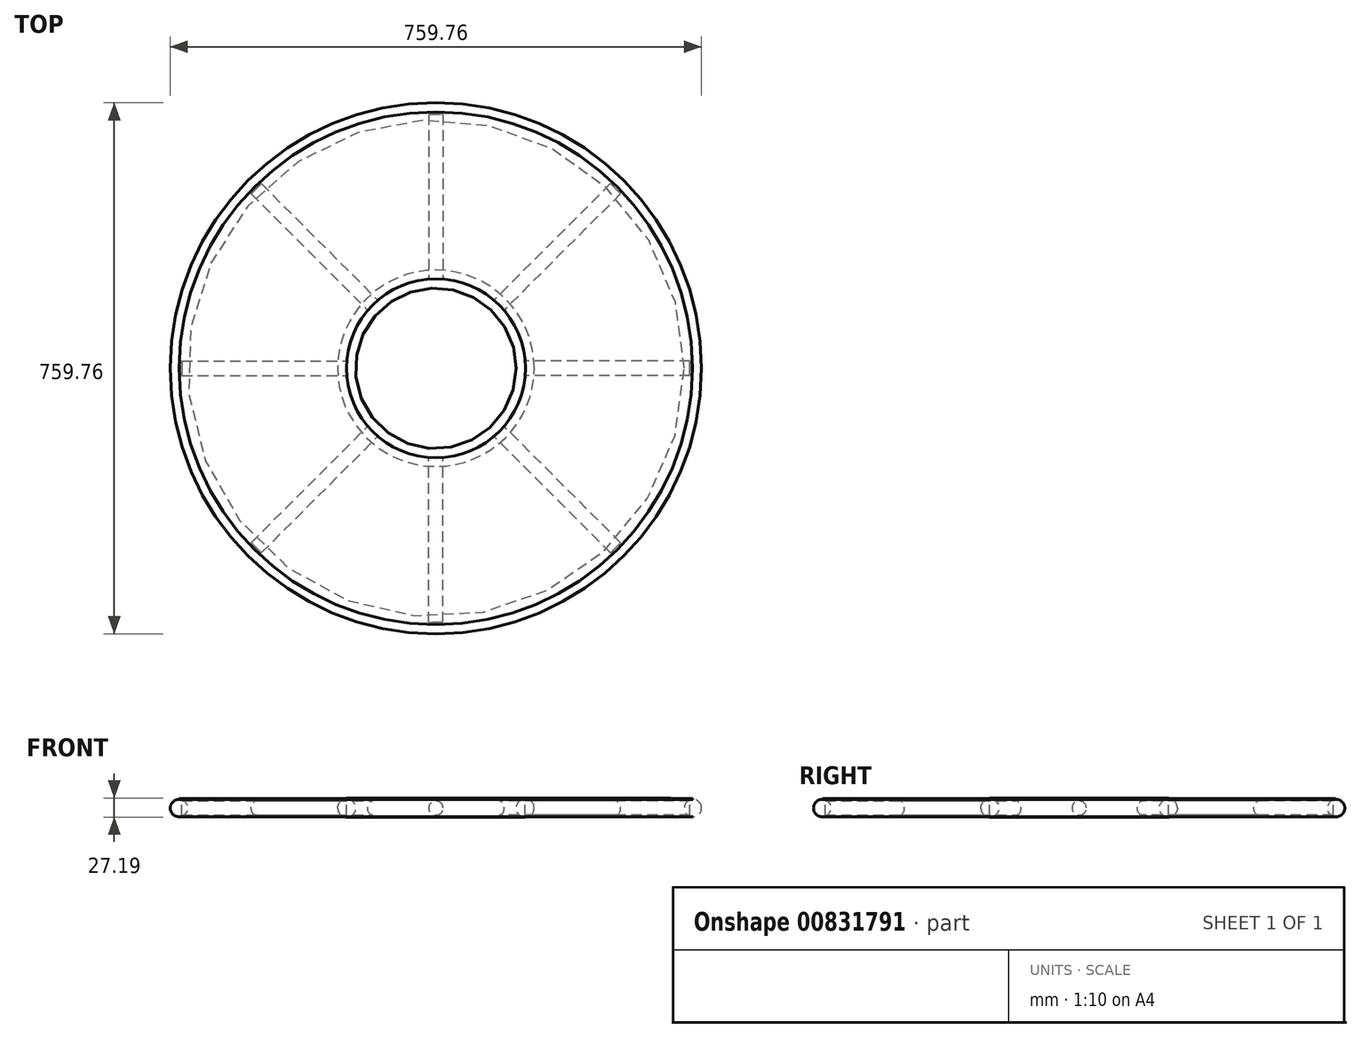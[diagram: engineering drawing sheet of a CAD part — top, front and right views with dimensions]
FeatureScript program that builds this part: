
annotation { "Feature Type Name" : "Feature", "Feature Type Description" : "" }
export const myFeature = defineFeature(function(context is Context, id is Id, definition is map)
    precondition{}
    {
        {
            var Q0;
            Q0=qCreatedBy(makeId("Front.planeOp"),FACE);
            var sketch = newSketch(context, id + "F0", { "sketchPlane" : qUnion([Q0])});
            skLineSegment(sketch, "E0", {"start": v(0, 74.1) * mm, "end": v(0, -371.99) * mm});
            skLineSegment(sketch, "E1.0", {"start": v(-115, 74.1) * mm, "end": v(-115, -373.98) * mm});
            skLineSegment(sketch, "E2.0", {"start": v(-380, 74.1) * mm, "end": v(-380, -371.99) * mm});
            skLineSegment(sketch, "E3", {"start": v(-423.99, 0) * mm, "end": v(0, 0) * mm});
            skLineSegment(sketch, "E4.0", {"start": v(-127.5, 74.1) * mm, "end": v(-127.5, -373.98) * mm});
            skLineSegment(sketch, "E5.0", {"start": v(-367.5, 74.1) * mm, "end": v(-367.5, -371.99) * mm});
            skSolve(sketch);
        }
        {
            var Q0;
            Q0=qCreatedBy(makeId("Front.planeOp"),FACE);
            var sketch = newSketch(context, id + "F1", { "sketchPlane" : qUnion([Q0])});
            skCircle(sketch, "E6", {"center": v(-127.64, 0) * mm, "radius": 12.85 * mm});
            skCircle(sketch, "E7", {"center": v(-367.53, 0) * mm, "radius": 12.34 * mm});
            skLineSegment(sketch, "E8", {"start": v(-366.89, 12.33) * mm, "end": v(-127.97, 12.84) * mm});
            skLineSegment(sketch, "E9.0", {"start": v(-366.9, 13.83) * mm, "end": v(-127.97, 14.34) * mm});
            skLineSegment(sketch, "E10", {"start": v(-127.97, 14.34) * mm, "end": v(-127.97, 12.84) * mm});
            skLineSegment(sketch, "E11", {"start": v(-366.9, 13.83) * mm, "end": v(-366.89, 12.33) * mm});
            skSolve(sketch);
        }
        {
            var Q0;
            Q0=makeQuery(id+"F1.imprint","IMPRINT",FACE,{"disambiguationData":[TD([[makeQuery(id+"F1.imprint","IMPRINT",EDGE,{"derivedFrom":sQuery(id+"F1.wireOp",EDGE,"E7")}),1.0]])]});
            var Q1;
            Q1=makeQuery(id+"F1.imprint","IMPRINT",FACE,{"disambiguationData":[TD([[makeQuery(id+"F1.imprint","IMPRINT",EDGE,{"derivedFrom":sQuery(id+"F1.wireOp",EDGE,"E8")}),1.0]])]});
            var Q2;
            Q2=makeQuery(id+"F1.imprint","IMPRINT",FACE,{"disambiguationData":[TD([[makeQuery(id+"F1.imprint","IMPRINT",EDGE,{"derivedFrom":sQuery(id+"F1.wireOp",EDGE,"E6")}),1.0]])]});
            var Q3;
            Q3=sQuery(id+"F0.wireOp",EDGE,"E0");
            revolve(context, id + "F2", {"surfaceOperationType" : NewSurfaceOperationType.NEW, "entities" : qUnion([Q0, Q1, Q2]), "axis" : qUnion([Q3]), "revolveType" : RevolveType.FULL});
        }
        {
            var Q0;
            Q0=qCreatedBy(makeId("Right.planeOp"),FACE);
            var sketch = newSketch(context, id + "F3", { "sketchPlane" : qUnion([Q0])});
            skCircle(sketch, "E12", {"center": v(0, 0) * mm, "radius": 10.23 * mm});
            skSolve(sketch);
        }
        {
            var Q0;
            Q0 = qSketchRegion(id + "F3", true);
            extrude(context, id + "F4", {"entities" : qUnion([Q0]), "depth" : 363.35 * mm, "offsetDistance" : 25 * mm, "hasSecondDirection" : true, "secondDirectionOppositeDirection" : false, "secondDirectionDepth" : 127.76 * mm});
        }
        {
            var Q0;
            Q0=makeQuery(id+"F4.opExtrude","SWEPT_BODY",BODY,{"disambiguationData":[OSD([sQuery(id+"F3.wireOp",EDGE,"E12")])]});
            var Q1;
            Q1=sQuery(id+"F0.wireOp",EDGE,"E0");
            circularPattern(context, id + "F5", {"entities" : qUnion([Q0]), "axis" : qUnion([Q1]), "angle" : 360 * degree, "instanceCount" : 8, "equalSpace" : true});
        }
    });
